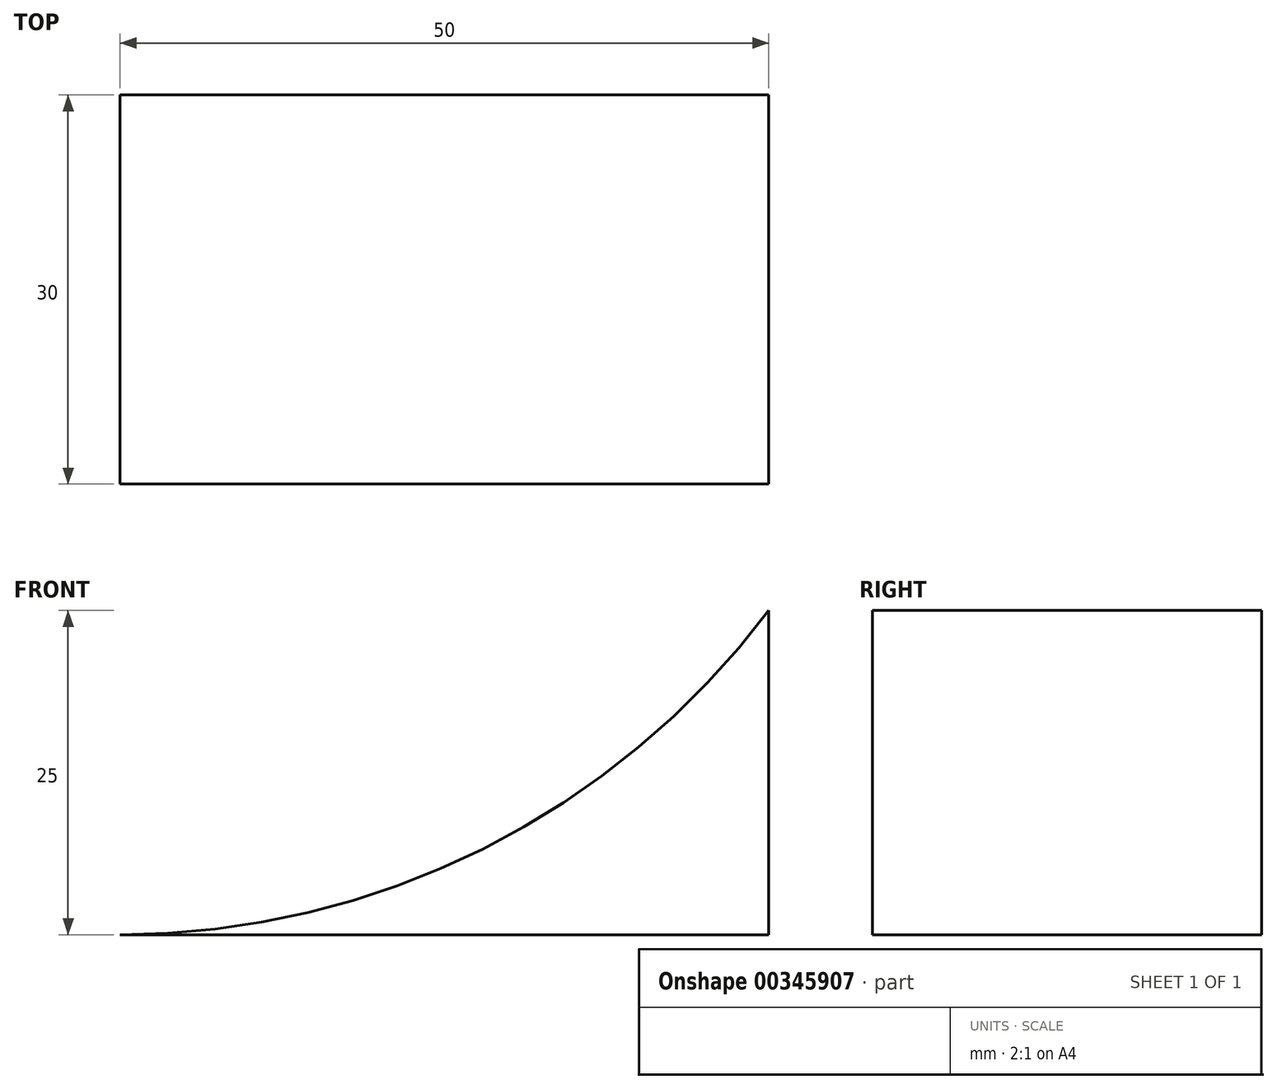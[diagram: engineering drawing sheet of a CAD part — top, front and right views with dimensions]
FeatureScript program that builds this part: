
annotation { "Feature Type Name" : "Feature", "Feature Type Description" : "" }
export const myFeature = defineFeature(function(context is Context, id is Id, definition is map)
    precondition{}
    {
        {
            var Q0;
            Q0=qCreatedBy(makeId("Front.planeOp"),FACE);
            var sketch = newSketch(context, id + "F0", { "sketchPlane" : qUnion([Q0])});
            skLineSegment(sketch, "E0", {"start": v(0, 0) * mm, "end": v(50, 0) * mm});
            skLineSegment(sketch, "E1", {"start": v(50, 0) * mm, "end": v(50, 25) * mm});
            skArc(sketch, "E2", {"start": v(0, 0) * mm, "mid": v(27.95, 6.6) * mm, "end": v(50, 25) * mm});
            skSolve(sketch);
        }
        {
            var Q0;
            Q0 = qSketchRegion(id + "F0", true);
            extrude(context, id + "F1", {"entities" : qUnion([Q0]), "depth" : 30 * mm});
        }
    });
